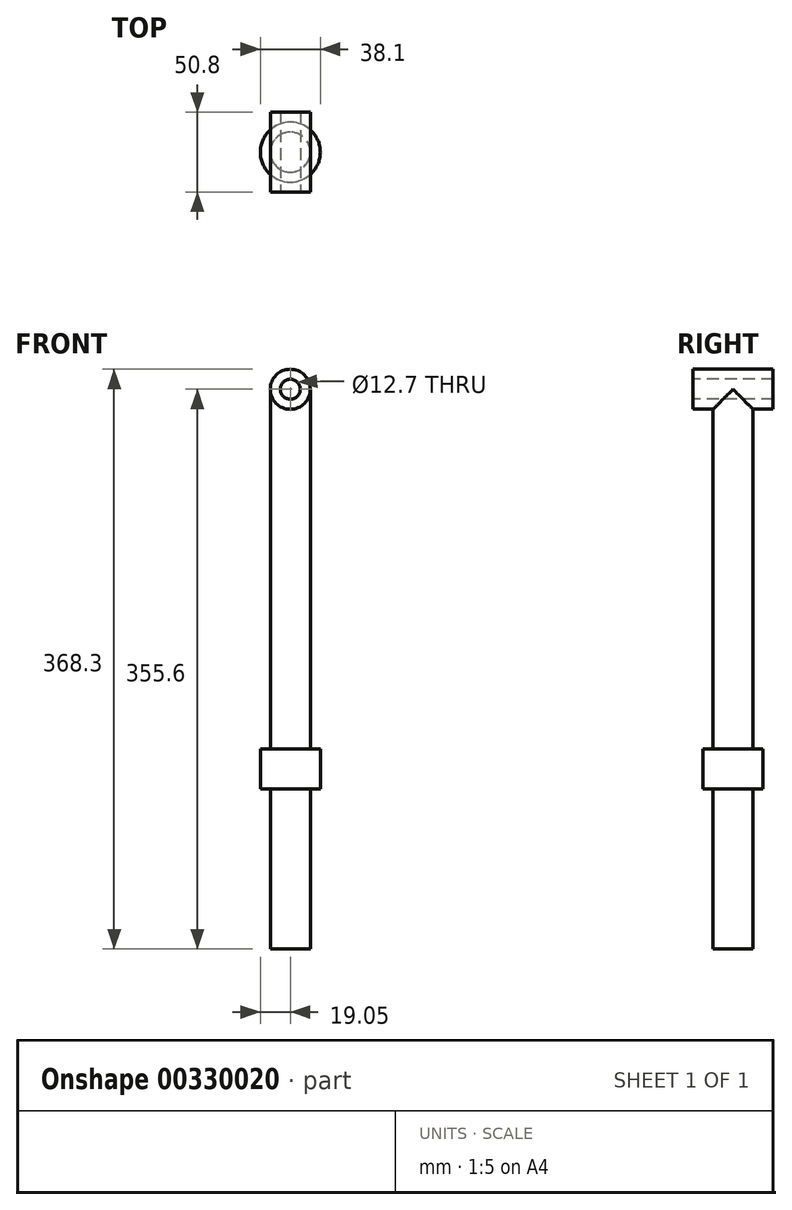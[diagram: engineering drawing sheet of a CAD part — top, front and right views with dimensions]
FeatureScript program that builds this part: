
annotation { "Feature Type Name" : "Feature", "Feature Type Description" : "" }
export const myFeature = defineFeature(function(context is Context, id is Id, definition is map)
    precondition{}
    {
        {
            var Q0;
            Q0=qCreatedBy(makeId("Top.planeOp"),FACE);
            var sketch = newSketch(context, id + "F0", { "sketchPlane" : qUnion([Q0])});
            skCircle(sketch, "E0", {"center": v(0, 0) * mm, "radius": 12.7 * mm});
            skSolve(sketch);
        }
        {
            var Q0;
            Q0=makeQuery(id+"F0.imprint","IMPRINT",FACE,{"disambiguationData":[TD([[makeQuery(id+"F0.imprint","IMPRINT",EDGE,{"derivedFrom":sQuery(id+"F0.wireOp",EDGE,"E0")}),1.0]])]});
            extrude(context, id + "F1", {"entities" : qUnion([Q0]), "oppositeDirection" : true, "depth" : 330.2 * mm, "hasSecondDirection" : true, "secondDirectionOppositeDirection" : false, "secondDirectionDepth" : 25.4 * mm});
        }
        {
            var Q0;
            Q0=qCreatedBy(makeId("Top.planeOp"),FACE);
            cPlane(context, id + "F2", {"entities" : qUnion([Q0]), "cplaneType" : CPlaneType.OFFSET, "offset" : 203.2 * mm, "oppositeDirection" : true, "width" : 152.4 * mm, "height" : 152.4 * mm});
        }
        {
            var Q0;
            Q0=qCreatedBy(id+"F2.planeOp",FACE);
            var sketch = newSketch(context, id + "F3", { "sketchPlane" : qUnion([Q0])});
            skCircle(sketch, "E1", {"center": v(0, 0) * mm, "radius": 19.05 * mm});
            skSolve(sketch);
        }
        {
            var Q0;
            Q0 = qSketchRegion(id + "F3", true);
            extrude(context, id + "F4", {"entities" : qUnion([Q0]), "operationType" : NewBodyOperationType.ADD, "oppositeDirection" : true, "depth" : 25.4 * mm});
        }
        {
            var Q0;
            Q0=qCreatedBy(makeId("Front.planeOp"),FACE);
            var sketch = newSketch(context, id + "F5", { "sketchPlane" : qUnion([Q0])});
            skCircle(sketch, "E2", {"center": v(0, 25.4) * mm, "radius": 12.7 * mm});
            skSolve(sketch);
        }
        {
            var Q0;
            Q0 = qSketchRegion(id + "F5", true);
            extrude(context, id + "F6", {"entities" : qUnion([Q0]), "operationType" : NewBodyOperationType.ADD, "depth" : 25.4 * mm, "hasSecondDirection" : true, "secondDirectionOppositeDirection" : true, "secondDirectionDepth" : 25.4 * mm});
        }
        {
            var Q0;
            Q0=qCreatedBy(makeId("Front.planeOp"),FACE);
            var sketch = newSketch(context, id + "F7", { "sketchPlane" : qUnion([Q0])});
            skCircle(sketch, "E3", {"center": v(0, 25.4) * mm, "radius": 6.35 * mm});
            skSolve(sketch);
        }
        {
            var Q0;
            Q0 = qSketchRegion(id + "F7", true);
            extrude(context, id + "F8", {"entities" : qUnion([Q0]), "operationType" : NewBodyOperationType.REMOVE, "endBound" : BoundingType.THROUGH_ALL, "oppositeDirection" : true, "depth" : 25.4 * mm, "hasSecondDirection" : true, "secondDirectionBound" : SecondDirectionBoundingType.THROUGH_ALL, "secondDirectionOppositeDirection" : false, "secondDirectionDepth" : 25.4 * mm});
        }
    });
